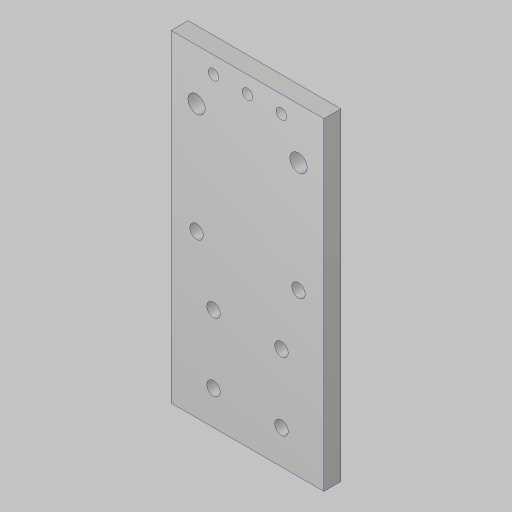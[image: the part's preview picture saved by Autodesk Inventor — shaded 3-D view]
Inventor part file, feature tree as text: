
AUTODESK INVENTOR PART (.ipt)
format: ipt  version: 2023.5 (Build 275446000, 446)  size: 264,704 bytes
history: native  units: in
note: dims shown in document units (in); Inventor stores cm internally (conversion verified against a paired STEP export)
features: hole x3, sketch x2, extrude x1
ambient origin geometry x8: Origin, YZ Plane, XZ Plane, XY Plane, X Axis, Y Axis, Z Axis, Center Point
bodies: Solid1 (feature_tree)
feature tree (6):
  sketch  "Sketch1"  dims[d0=0.257in d1=1.5in]
  extrude  "Extrusion1"  Depth=1.5in
  hole  "Hole1"  [1 undecoded]
  hole  "Hole2"  [1 undecoded]
  hole  "Hole3"  [1 undecoded]
  sketch  "Sketch2"  dims[d4=4.0in d6=0.25in d7=0.0in d8=1.5in d9=2.375in d10=0.201in d11=0.75in d12=0.385in d13=0.25in d14=0.5635in d15=1.0in d16=0.8108in d17=6.0in d18=2.25in d19=0.25in d20=4.75in d21=1.0in d22=0.156in d23=0.38in d24=0.385in d25=0.25in d26=0.5635in d27=1.0in d28=0.8108in d29=0.25in d32=1.0in d33=1.0in d34=0.5in d35=0.201in d36=0.38in d37=0.385in d38=0.25in d39=0.5635in d40=1.0in d41=0.8108in]
note: 3 required parameter values undecoded (feature->parameter linkage not recoverable at this tier; creation-order binding heuristic only, values carry confidence <= 0.55)
